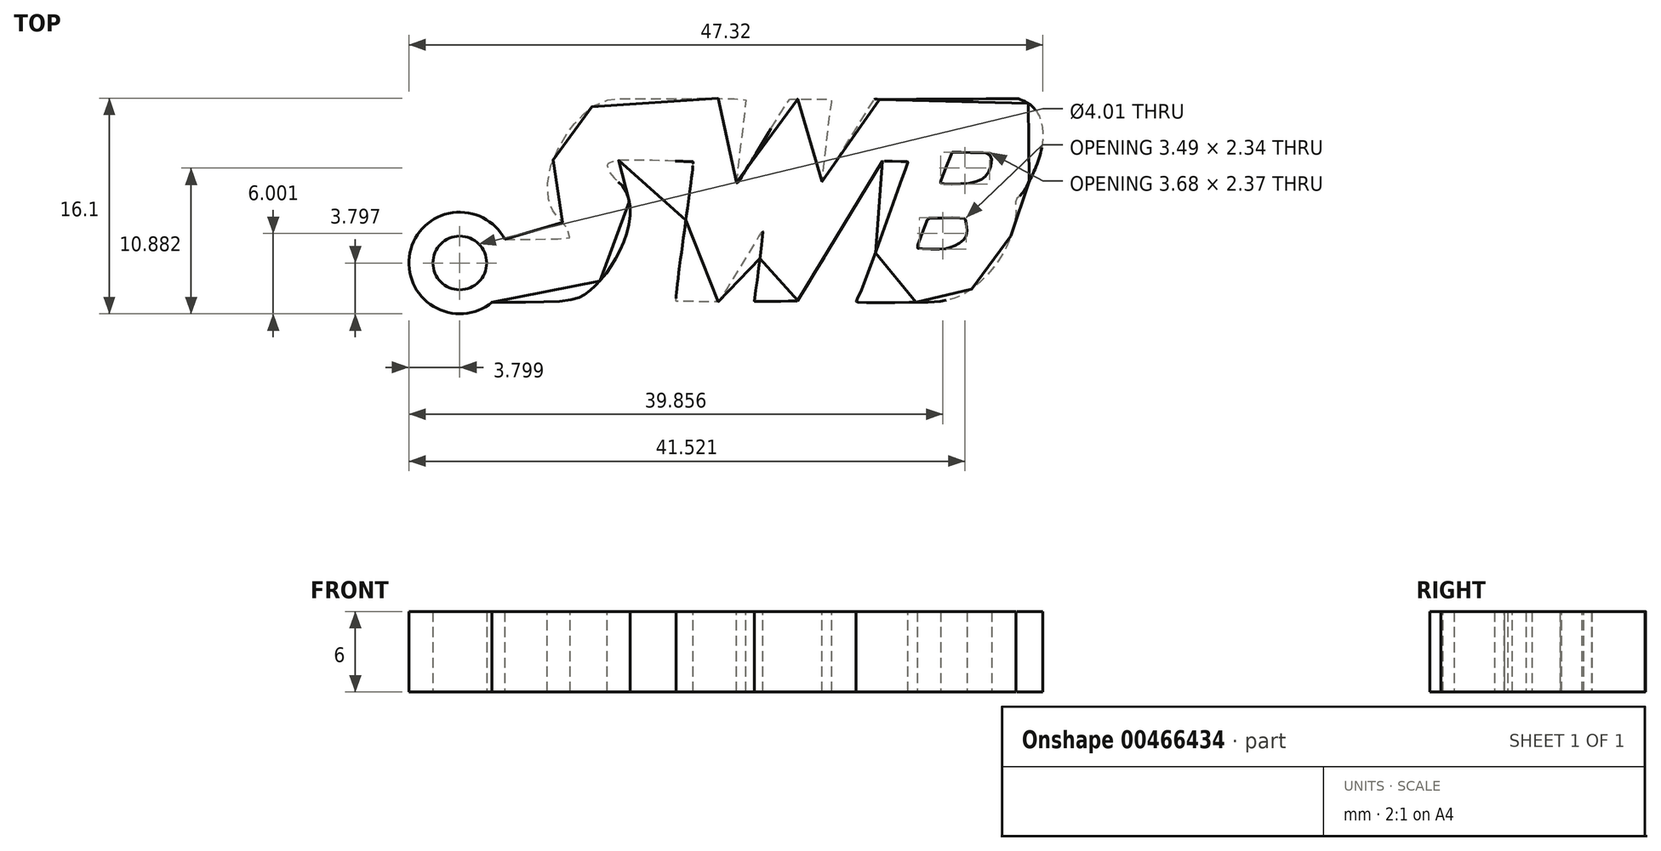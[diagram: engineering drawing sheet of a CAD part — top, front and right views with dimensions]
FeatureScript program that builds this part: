
annotation { "Feature Type Name" : "Feature", "Feature Type Description" : "" }
export const myFeature = defineFeature(function(context is Context, id is Id, definition is map)
    precondition{}
    {
        {
            var Q0;
            Q0=qCreatedBy(makeId("Top.planeOp"),FACE);
            var sketch = newSketch(context, id + "F0", { "sketchPlane" : qUnion([Q0])});
            skFitSpline(sketch, "E0", {"points": [v(3.16, 14.03) * mm, v(13.88, 14.06) * mm, v(13.97, 14.04) * mm, v(14.4, 13.86) * mm, v(15.33, 12.97) * mm, v(15.66, 10.6) * mm, v(14.73, 7.97) * mm, v(14.04, 6.85) * mm, v(13.7, 6.5) * mm, v(13.7, 5.77) * mm, v(13.45, 4.18) * mm, v(12.74, 2.51) * mm, v(11.7, 1.05) * mm, v(10.8, 0.2) * mm, v(10.3, -0.23) * mm, v(9.41, -0.74) * mm, v(8.73, -0.94) * mm, v(7.73, -1.1) * mm, v(6.02, -1.13) * mm, v(1.83, -1.13) * mm, v(1.78, -1.1) * mm, v(1.95, -0.74) * mm, v(5.62, 9.32) * mm, v(5.63, 9.38) * mm, v(5.37, 9.38) * mm, v(3.73, 9.4) * mm, v(3.68, 9.37) * mm, v(3.59, 9.21) * mm, v(-2.57, -0.96) * mm, v(-2.65, -1.04) * mm, v(-2.85, -1.04) * mm, v(-5.79, -1.07) * mm, v(-5.82, -1.06) * mm, v(-5.82, -0.98) * mm, v(-5.2, 4.15) * mm, v(-5.21, 4.15) * mm, v(-5.26, 4.12) * mm, v(-8.47, -1.08) * mm, v(-8.5, -1.1) * mm, v(-8.6, -1.1) * mm, v(-11.57, -1.06) * mm, v(-11.63, -1.06) * mm, v(-11.67, -0.98) * mm, v(-10.4, 9.35) * mm, v(-10.42, 9.36) * mm, v(-10.48, 9.36) * mm, v(-15.99, 9.45) * mm, v(-16.28, 9.37) * mm, v(-16.77, 9.16) * mm, v(-16.3, 8.15) * mm, v(-15.5, 7.3) * mm, v(-15.09, 5.36) * mm, v(-15.78, 2.9) * mm, v(-17.01, 0.85) * mm, v(-18.27, -0.4) * mm, v(-20.1, -1.03) * mm, v(-26.55, -1.15) * mm, v(-26.6, -1.15) * mm, v(-26.27, 0.08) * mm, v(-25.61, 3.28) * mm, v(-25.52, 3.56) * mm, v(-24.89, 3.57) * mm, v(-20.42, 3.59) * mm, v(-19.58, 3.7) * mm, v(-19.78, 4.4) * mm, v(-20.47, 5.16) * mm, v(-20.93, 5.8) * mm, v(-21.25, 6.88) * mm, v(-21.02, 9.04) * mm, v(-20.03, 11.1) * mm, v(-19.37, 12.05) * mm, v(-18.6, 12.9) * mm, v(-17.67, 13.62) * mm, v(-16.46, 14.05) * mm, v(-16.14, 14.06) * mm, v(-6.55, 14.04) * mm, v(-6.46, 14) * mm, v(-6.46, 13.75) * mm, v(-7.16, 7.84) * mm, v(-7.14, 7.78) * mm, v(-7.07, 7.82) * mm, v(-3.23, 13.99) * mm, v(-3.16, 14.04) * mm, v(-3.03, 14.05) * mm, v(-0.1, 14.03) * mm, v(-0.06, 13.94) * mm, v(-0.77, 7.9) * mm, v(-0.76, 7.84) * mm, v(-0.67, 7.94) * mm, v(3.07, 13.93) * mm, v(3.12, 14) * mm, v(3.14, 14.03) * mm, v(3.16, 14.03) * mm]});
            skFitSpline(sketch, "E1", {"points": [v(10.92, 10.04) * mm, v(11.38, 10.03) * mm, v(11.84, 9.78) * mm, v(11.71, 8.7) * mm, v(11.12, 8.04) * mm, v(9.68, 7.72) * mm, v(8.09, 7.76) * mm, v(8.07, 7.8) * mm, v(8.1, 7.94) * mm, v(8.93, 10.04) * mm, v(8.94, 10.06) * mm, v(9, 10.07) * mm, v(10.92, 10.04) * mm]});
            skFitSpline(sketch, "E2", {"points": [v(9.94, 5.06) * mm, v(10.03, 4.06) * mm, v(9.67, 3.42) * mm, v(8.9, 3) * mm, v(8.13, 2.83) * mm, v(6.39, 2.9) * mm, v(6.35, 3) * mm, v(7.16, 5.12) * mm, v(7.28, 5.16) * mm, v(9.21, 5.17) * mm, v(9.9, 5.1) * mm, v(9.94, 5.06) * mm]});
            skPoint(sketch, "E3.third.point", {"position": v(-31.84, 1.66) * mm});
            skPoint(sketch, "E4.third.point", {"position": v(-31.32, 3.28) * mm});
            skCircle(sketch, "E5", {"center": v(-27.81, 1.8) * mm, "radius": 3.8 * mm});
            skCircle(sketch, "E6", {"center": v(-27.81, 1.8) * mm, "radius": 2 * mm});
            skSolve(sketch);
        }
        {
            var Q0;
            Q0=makeQuery(id+"F0.imprint","IMPRINT",FACE,{"disambiguationData":[TD([[makeQuery(id+"F0.imprint","IMPRINT",EDGE,{"derivedFrom":sQuery(id+"F0.wireOp",EDGE,"E0")}),-1.0]])]});
            extrude(context, id + "F1", {"entities" : qUnion([Q0]), "depth" : 6 * mm, "offsetDistance" : 25 * mm});
        }
        {
            var Q0;
            Q0 = qSketchRegion(id + "F0", true);
            extrude(context, id + "F2", {"entities" : qUnion([Q0]), "operationType" : NewBodyOperationType.ADD, "depth" : 6 * mm, "offsetDistance" : 25 * mm});
        }
    });
